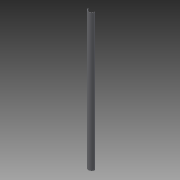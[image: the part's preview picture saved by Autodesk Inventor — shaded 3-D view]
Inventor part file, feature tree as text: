
AUTODESK INVENTOR PART (.ipt)
format: ipt  version: 2015 SP1 (Build 190203100, 203)  size: 95,744 bytes
history: native  units: mm
features: extrude x2, sketch x2, mirror x1
ambient origin geometry x8: Origin, YZ Plane, XZ Plane, XY Plane, X Axis, Y Axis, Z Axis, Center Point
bodies: Solid1 (feature_tree)
feature tree (5):
  extrude  "Extrusion1"  Depth=100.0mm
  extrude  "Extrusion2"  Depth=10.0mm
  mirror  "Mirror1"
  sketch  "Sketch1"  dims[d0=3.0mm d1=100.0mm]
  sketch  "Sketch2"  dims[d2=2000.0mm d3=0.0mm d4=4.0mm d5=20.0mm d6=10.0mm d7=0.0mm d8=0.0mm]
